# Revit family: Firestop-Wrap_Strip-STI-Series_SS_WBLU2_Sealant_6_to_12_wall
name_source: partatom
category: Specialty Equipment
units: mm (PartAtom-declared; Revit-internal decimal feet)

## family parameters
Always vertical = Yes
Classification Number = 23.20.50.14.11
Cut with Voids When Loaded = No
Enable Cutting in Views = No
Host = Wall
Maintain Annotation Orientation = No
Part Type = Normal
Room Calculation Point = No
Round Connector Dimension = Use Diameter
Shared = No

## types (4) — shared parameters
Assembly Code = D4030900
Default Elevation = 0' - 0"
Description = BLU2 Wrap Strip (2" X 1/8" X 12')
Fire Rating = Up to 4 Hr
Firestop-STI-Intumescent-Blue = RAP BULE
Galvanized-STI-Steel-Collar = Collar
Green Building/LEED® Information = http://sti.fmpdata.net
Guide Specification = http://www.stifirestop.com
Locate Distributor = http://www.stifirestop.com
MSDS = http://files.systems.stifirestop.com
Manufacturer = Specified Technologies Inc.
Manufacturer Fax No. = 908.526.9623
Model = SSWBLU2
Mounting tabs large Width = 0' - 1"
Mounting tabs small Width = 0' - 0 1/2"
Product Documentation Link = http://files.systems.stifirestop.com
Product Page URL = http://www.stifirestop.com
Screw hole Width = 0' - 0 3/8"
Tested Systems = http://sti.fmpdata.net
URL = http://www.stifirestop.com

## per-type parameters (varying)
| type | Color | ID of Collar | Material | Mounting tab ID | Pipe OD | Stack Height |
| 06 Pipe |  | 0' - 7 3/8" |  | 0' - 3 5/8" | 0' - 6 5/8" | 0' - 4" |
| 08 Pipe |  | 0' - 9 5/8" |  | 0' - 4 3/4" | 0' - 8 5/8" | 0' - 4" |
| 10 pipe |  | 0' - 11 3/4" |  | 0' - 5 13/16" | 0' - 10 3/4" | 0' - 5" |
| 12 Pipe | BLUE | 1' - 2" | Flexible intumescent strip faced with plastic | 0' - 6 15/16" | 1' - 0 3/4" | 0' - 5" |

## geometry (parser evidence)
native form markers: Blend x14, Sweep x3
no freeform markers — native parametric forms only
